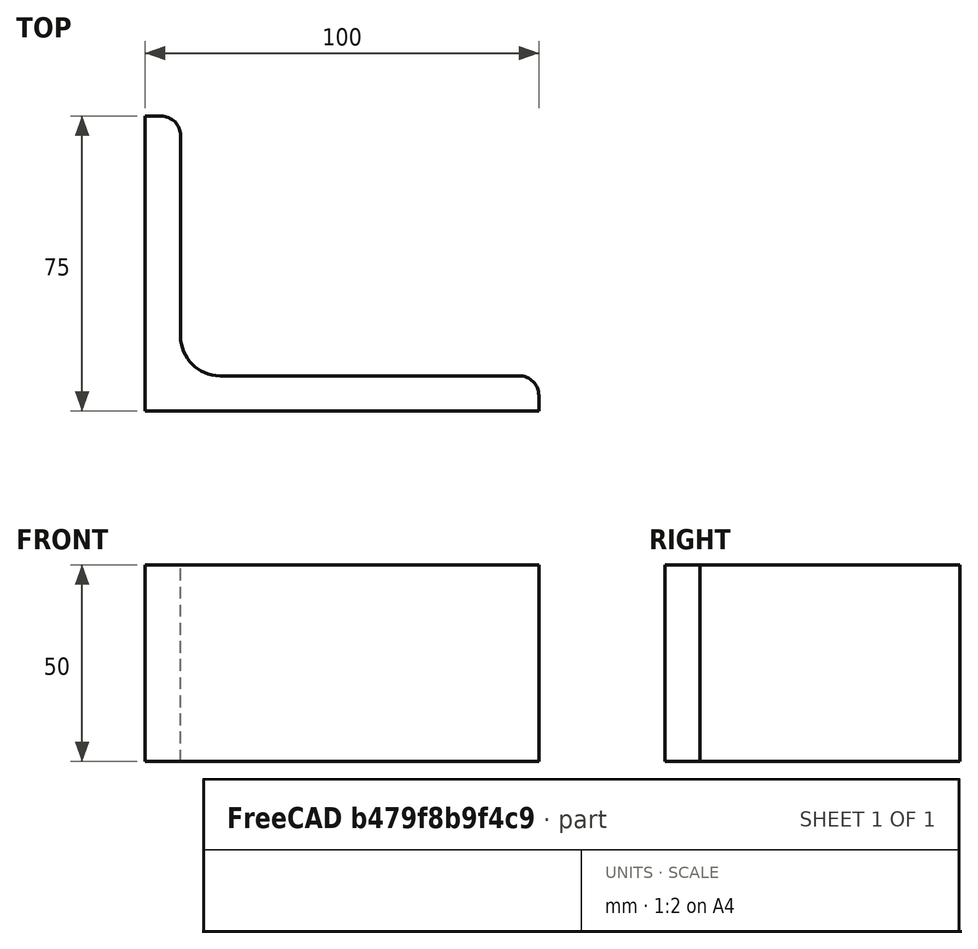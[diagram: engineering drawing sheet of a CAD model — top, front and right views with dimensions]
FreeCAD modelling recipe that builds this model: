
FCSTD DOCUMENT  (FreeCAD 0.15R4671 (Git))
Label: Angle Bar 100x75x9 EN10056 S235JR
License: All rights reserved
LicenseURL: http://en.wikipedia.org/wiki/All_rights_reserved
objects: Sketcher::SketchObject×1, Part::Extrusion×1
note: 2 computed .brp shape members not serialized (recipe doc carries the construction recipe); baked Part::Feature solids carry a one-line shape summary decoded from their .brp

FEATURE [Sketcher::SketchObject] Sketch
  sketch-geometry (9):
    g0: LineSegment StartX=0 StartY=0 StartZ=0 EndX=100 EndY=0 EndZ=0
    g1: LineSegment StartX=100 StartY=0 StartZ=0 EndX=100 EndY=4 EndZ=0
    g2: LineSegment StartX=95 StartY=9 StartZ=0 EndX=19 EndY=9 EndZ=0
    g3: LineSegment StartX=0 StartY=0 StartZ=0 EndX=0 EndY=75 EndZ=0
    g4: LineSegment StartX=0 StartY=75 StartZ=0 EndX=4 EndY=75 EndZ=0
    g5: LineSegment StartX=9 StartY=70 StartZ=0 EndX=9 EndY=19 EndZ=0
    g6: ArcOfCircle CenterX=19 CenterY=19 CenterZ=0 NormalX=0 NormalY=0 NormalZ=1 Radius=10 StartAngle=3.14159 EndAngle=4.71239
    g7: ArcOfCircle CenterX=4 CenterY=70 CenterZ=0 NormalX=0 NormalY=0 NormalZ=1 Radius=5 StartAngle=0 EndAngle=1.5708
    g8: ArcOfCircle CenterX=95 CenterY=4 CenterZ=0 NormalX=0 NormalY=0 NormalZ=1 Radius=5 StartAngle=0 EndAngle=1.5708
  constraints (23):
    c: Coincident(g0,g-1)
    c: Horizontal(g0)
    c: Coincident(g1,g0)
    c: Vertical(g1)
    c: Horizontal(g2)
    c: Coincident(g3,g-1)
    c: Vertical(g3)
    c: Coincident(g4,g3)
    c: Horizontal(g4)
    c: Vertical(g5)
    c: Tangent(g5,g6) = -1.5708
    c: Tangent(g2,g6) = 1.5708
    c: Tangent(g4,g7) = 1.5708
    c: Tangent(g5,g7) = 1.5708
    c: Tangent(g2,g8) = -1.5708
    c: Tangent(g1,g8) = -1.5708
    c: DistanceX(g0) = 100
    c: DistanceY(g3) = 75
    c: DistanceY(g0,g2) = 9
    c: DistanceX(g3,g5) = 9
    c: Radius(g6) = 10
    c: Radius(g8) = 5
    c: Radius(g7) = 5
FEATURE [Part::Extrusion] Extrude  label="Angle Bar 100x75x9 EN10056 S235JR"
  Base = -> Sketch
  Dir = (0,0,50)
  Solid = true
